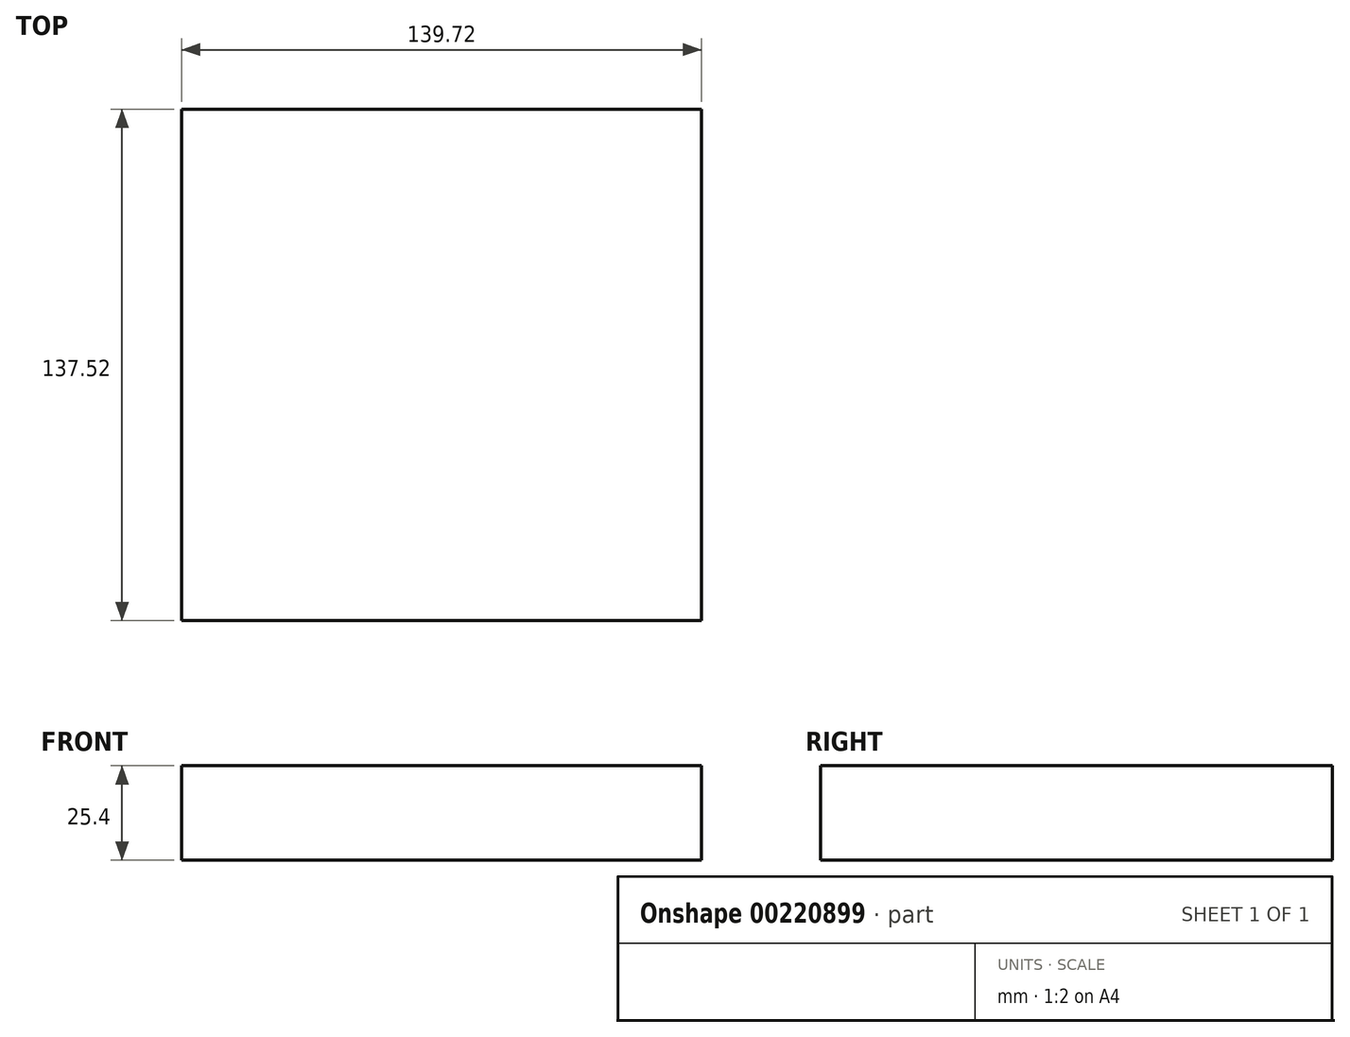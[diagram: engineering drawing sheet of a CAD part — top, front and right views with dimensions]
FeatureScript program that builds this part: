
annotation { "Feature Type Name" : "Feature", "Feature Type Description" : "" }
export const myFeature = defineFeature(function(context is Context, id is Id, definition is map)
    precondition{}
    {
        {
            var Q0;
            Q0=qCreatedBy(makeId("Top.planeOp"),FACE);
            var sketch = newSketch(context, id + "F0", { "sketchPlane" : qUnion([Q0])});
            skLineSegment(sketch, "E0.bottom", {"start": v(69.86, -68.76) * mm, "end": v(-69.86, -68.76) * mm});
            skLineSegment(sketch, "E0.top", {"start": v(69.86, 68.76) * mm, "end": v(-69.86, 68.76) * mm});
            skLineSegment(sketch, "E0.left", {"start": v(69.86, -68.76) * mm, "end": v(69.86, 68.76) * mm});
            skLineSegment(sketch, "E0.right", {"start": v(-69.86, -68.76) * mm, "end": v(-69.86, 68.76) * mm});
            skPoint(sketch, "E0.middle", {"position": v(0, 0) * mm});
            skLineSegment(sketch, "E1", {"start": v(0, 68.76) * mm, "end": v(0, -68.76) * mm});
            skSolve(sketch);
        }
        {
            var Q0;
            Q0=qCreatedBy(makeId("Top.planeOp"),FACE);
            var sketch = newSketch(context, id + "F1", { "sketchPlane" : qUnion([Q0])});
            skCircle(sketch, "E2", {"center": v(54.26, 0) * mm, "radius": 9.82 * mm});
            skSolve(sketch);
        }
        {
            var Q0;
            Q0=sQuery(id+"F1.wireOp",EDGE,"E2");
            var Q1;
            Q1=sQuery(id+"F0.wireOp",EDGE,"E1");
            revolve(context, id + "F2", {"bodyType" : ToolBodyType.SURFACE, "surfaceEntities" : qUnion([Q0]), "axis" : qUnion([Q1]), "revolveType" : RevolveType.ONE_DIRECTION, "angle" : 180 * degree});
        }
        {
            var Q0;
            Q0 = qSketchRegion(id + "F0", true);
            extrude(context, id + "F3", {"entities" : qUnion([Q0]), "depth" : 25.4 * mm});
        }
    });
